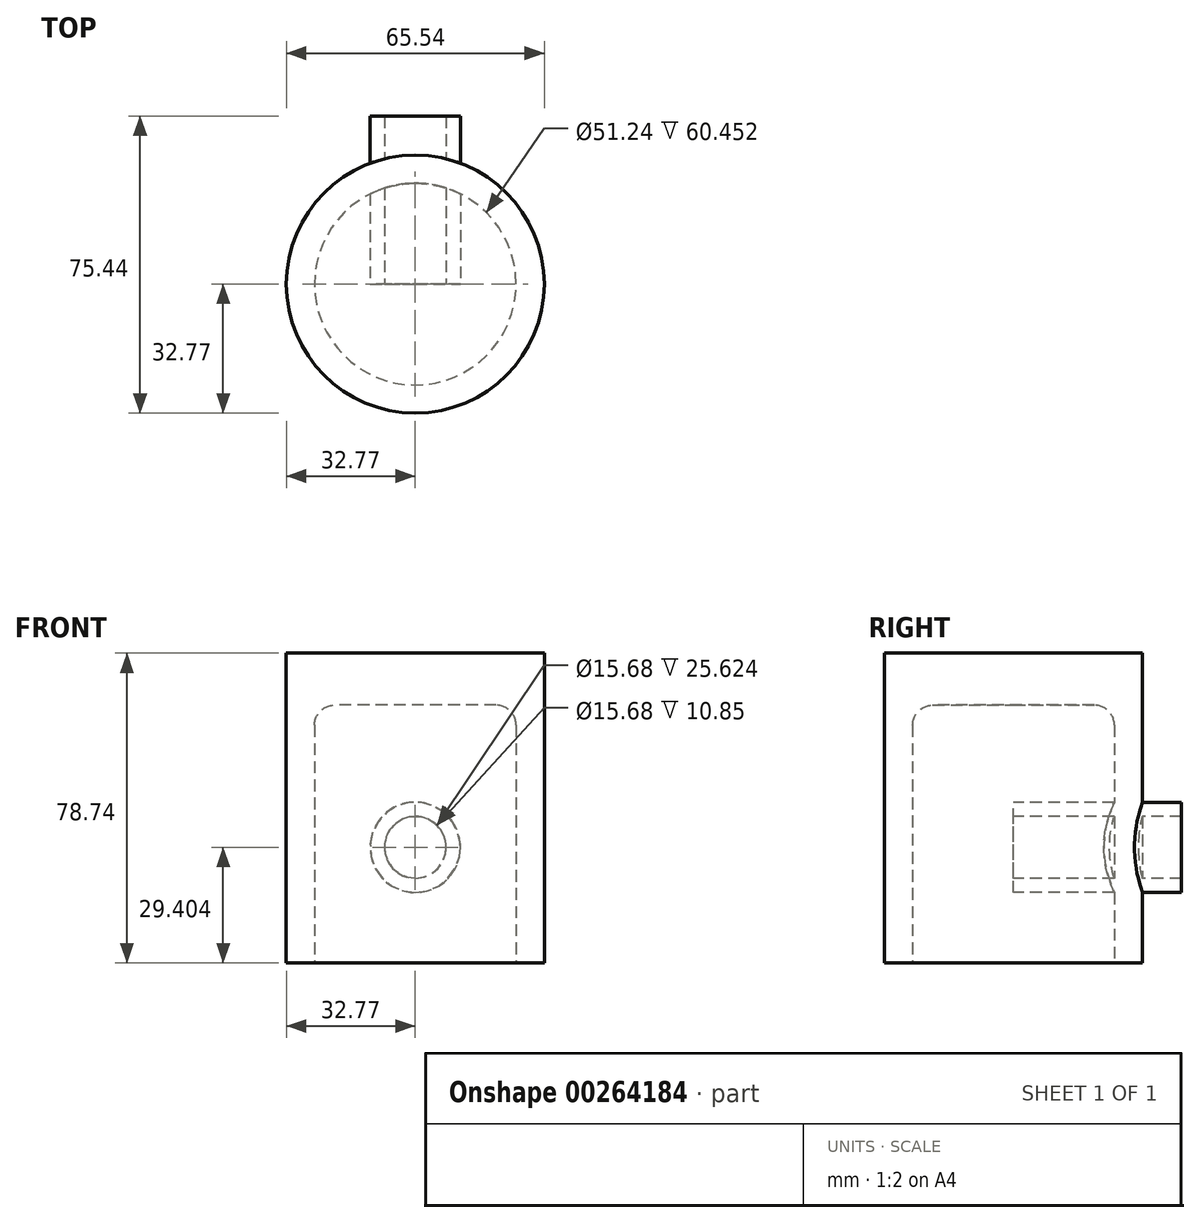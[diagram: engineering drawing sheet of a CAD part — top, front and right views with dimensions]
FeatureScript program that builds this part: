
annotation { "Feature Type Name" : "Feature", "Feature Type Description" : "" }
export const myFeature = defineFeature(function(context is Context, id is Id, definition is map)
    precondition{}
    {
        {
            var Q0;
            Q0=qCreatedBy(makeId("Top.planeOp"),FACE);
            var sketch = newSketch(context, id + "F0", { "sketchPlane" : qUnion([Q0])});
            skCircle(sketch, "E0", {"center": v(0, 0) * mm, "radius": 32.77 * mm});
            skSolve(sketch);
        }
        {
            var Q0;
            Q0=makeQuery(id+"F0.imprint","IMPRINT",FACE,{"disambiguationData":[TD([[makeQuery(id+"F0.imprint","IMPRINT",EDGE,{"derivedFrom":sQuery(id+"F0.wireOp",EDGE,"E0")}),1.0]])]});
            extrude(context, id + "F1", {"entities" : qUnion([Q0]), "depth" : 78.74 * mm});
        }
        {
            var Q0;
            Q0=qCreatedBy(makeId("Top.planeOp"),FACE);
            var sketch = newSketch(context, id + "F2", { "sketchPlane" : qUnion([Q0])});
            skCircle(sketch, "E1", {"center": v(0, 0) * mm, "radius": 25.62 * mm});
            skSolve(sketch);
        }
        {
            var Q0;
            Q0 = qSketchRegion(id + "F2", true);
            extrude(context, id + "F3", {"entities" : qUnion([Q0]), "operationType" : NewBodyOperationType.REMOVE, "depth" : 65.53 * mm});
        }
        {
            var Q0;
            Q0=makeQuery(id+"F3.boolean.opBoolean","COPY",EDGE,{"derivedFrom":makeQuery(id+"F3.opExtrude","CAP_EDGE",EDGE,{"disambiguationData":[OSD([sQuery(id+"F2.wireOp",EDGE,"E1")])],"isStart":true})});
            var Q1;
            Q1=makeQuery(id+"F3.boolean.opBoolean","COPY",EDGE,{"derivedFrom":makeQuery(id+"F3.opExtrude","CAP_EDGE",EDGE,{"disambiguationData":[OSD([sQuery(id+"F2.wireOp",EDGE,"E1")])],"isStart":false})});
            fillet(context, id + "F4", {"entities" : qUnion([Q0, Q1]), "radius" : 5.08 * mm, "tangentPropagation" : true, "allowEdgeOverflow" : false});
        }
        {
            var Q0;
            Q0=qCreatedBy(makeId("Front.planeOp"),FACE);
            var sketch = newSketch(context, id + "F5", { "sketchPlane" : qUnion([Q0])});
            skCircle(sketch, "E2", {"center": v(0, 29.4) * mm, "radius": 11.47 * mm});
            skCircle(sketch, "E3", {"center": v(0, 29.4) * mm, "radius": 7.84 * mm});
            skSolve(sketch);
        }
        {
            var Q0;
            Q0 = qSketchRegion(id + "F5", true);
            extrude(context, id + "F6", {"entities" : qUnion([Q0]), "operationType" : NewBodyOperationType.ADD, "oppositeDirection" : true, "depth" : 42.67 * mm});
        }
    });
